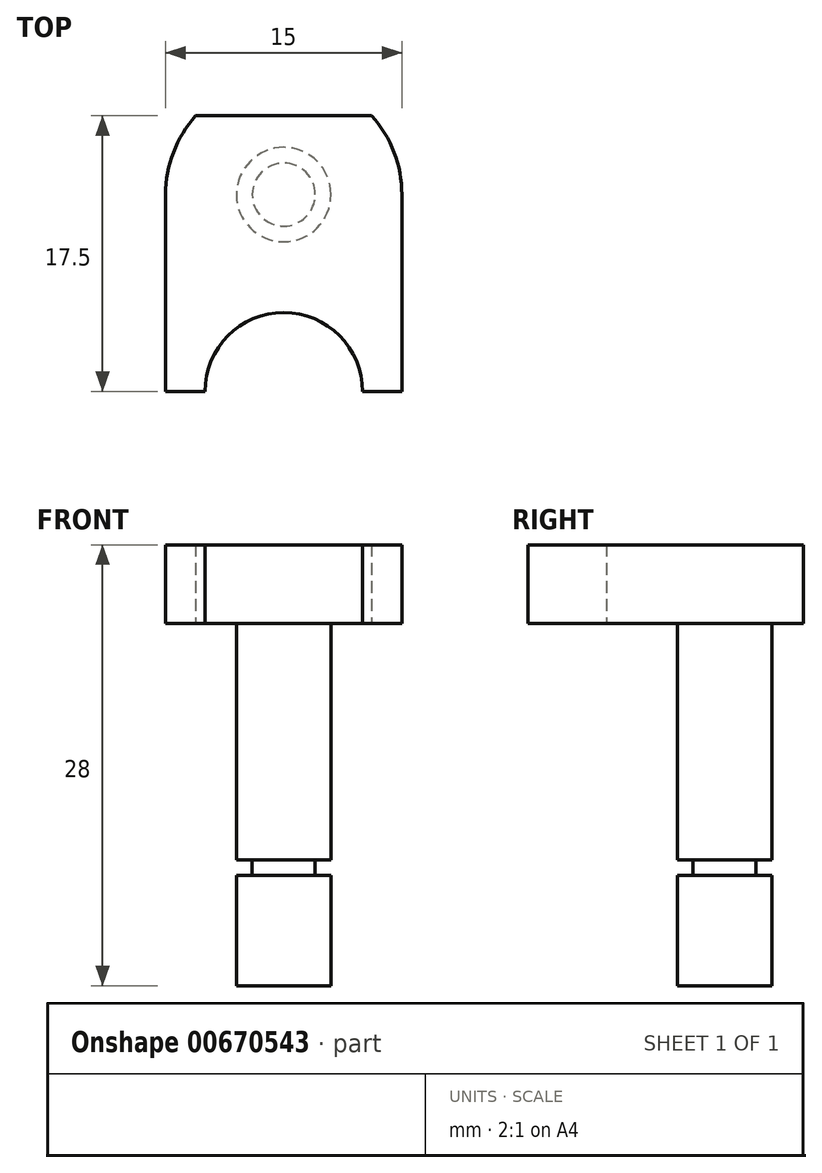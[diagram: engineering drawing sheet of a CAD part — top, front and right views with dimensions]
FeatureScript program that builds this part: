
annotation { "Feature Type Name" : "Feature", "Feature Type Description" : "" }
export const myFeature = defineFeature(function(context is Context, id is Id, definition is map)
    precondition{}
    {
        {
            var Q0;
            Q0=qCreatedBy(makeId("Top.planeOp"),FACE);
            var sketch = newSketch(context, id + "F0", { "sketchPlane" : qUnion([Q0])});
            skCircle(sketch, "E0", {"center": v(0, 0) * mm, "radius": 7.5 * mm});
            skLineSegment(sketch, "E1.bottom", {"start": v(-7.5, 5) * mm, "end": v(7.5, 5) * mm});
            skLineSegment(sketch, "E1.top", {"start": v(-7.5, -7.5) * mm, "end": v(7.5, -7.5) * mm});
            skLineSegment(sketch, "E1.left", {"start": v(-7.5, 5) * mm, "end": v(-7.5, -7.5) * mm});
            skLineSegment(sketch, "E1.right", {"start": v(7.5, 5) * mm, "end": v(7.5, -7.5) * mm});
            skArc(sketch, "E2", {"start": v(5, -12.5) * mm, "mid": v(0, -7.5) * mm, "end": v(-5, -12.5) * mm});
            skLineSegment(sketch, "E3", {"start": v(7.5, -12.5) * mm, "end": v(5, -12.5) * mm});
            skLineSegment(sketch, "E4", {"start": v(7.5, -12.5) * mm, "end": v(7.5, -7.5) * mm});
            skLineSegment(sketch, "E5", {"start": v(-7.5, -7.5) * mm, "end": v(-7.5, -12.5) * mm});
            skLineSegment(sketch, "E6", {"start": v(-7.5, -12.5) * mm, "end": v(-5, -12.5) * mm});
            skSolve(sketch);
        }
        {
            var Q0;
            Q0=makeQuery(id+"F0.imprint","IMPRINT",FACE,{"disambiguationData":[TD([[makeQuery(id+"F0.imprint","IMPRINT",EDGE,{"derivedFrom":sQuery(id+"F0.wireOp",EDGE,"E0")}),1.0]])]});
            var Q1;
            {var subQ0=sQuery(id+"F0.wireOp",EDGE,"E1.right");var subQ1=sQuery(id+"F0.wireOp",EDGE,"E0");var subQ2=makeQuery(id+"F0.imprint","INTERSECT",VERTEX,{"derivedFrom":[subQ1,subQ0]});Q1=makeQuery(id+"F0.imprint","IMPRINT",FACE,{"disambiguationData":[TD([[makeQuery(id+"F0.imprint","IMPRINT",EDGE,{"disambiguationData":[TD([[subQ2,1.0]])],"derivedFrom":subQ1}),-1.0]])]});}
            var Q2;
            {var subQ0=sQuery(id+"F0.wireOp",EDGE,"E1.left");var subQ1=sQuery(id+"F0.wireOp",EDGE,"E0");var subQ2=makeQuery(id+"F0.imprint","INTERSECT",VERTEX,{"derivedFrom":[subQ1,subQ0]});Q2=makeQuery(id+"F0.imprint","IMPRINT",FACE,{"disambiguationData":[TD([[makeQuery(id+"F0.imprint","IMPRINT",EDGE,{"disambiguationData":[TD([[subQ2,-1.0]])],"derivedFrom":subQ1}),-1.0]])]});}
            var Q3;
            {var subQ4=sQuery(id+"F0.wireOp",EDGE,"E3");Q3=makeQuery(id+"F0.imprint","IMPRINT",FACE,{"disambiguationData":[TD([[makeQuery(id+"F0.imprint","IMPRINT",EDGE,{"derivedFrom":subQ4}),-1.0]])]});}
            var Q4;
            {var subQ0=sQuery(id+"F0.wireOp",EDGE,"E5");Q4=makeQuery(id+"F0.imprint","IMPRINT",FACE,{"disambiguationData":[TD([[makeQuery(id+"F0.imprint","IMPRINT",EDGE,{"derivedFrom":subQ0}),1.0]])]});}
            extrude(context, id + "F1", {"entities" : qUnion([Q0, Q1, Q2, Q3, Q4]), "depth" : 5 * mm, "offsetDistance" : 25 * mm});
        }
        {
            var Q0;
            Q0=makeQuery(id+"F1.opExtrude","CAP_FACE",FACE,{"disambiguationData":[OSD([sQuery(id+"F0.wireOp",EDGE,"E0")])],"isStart":true});
            var sketch = newSketch(context, id + "F2", { "sketchPlane" : qUnion([Q0])});
            skCircle(sketch, "E7", {"center": v(0, 0) * mm, "radius": 3 * mm});
            skSolve(sketch);
        }
        {
            var Q0;
            Q0=makeQuery(id+"F2.imprint","IMPRINT",FACE,{"disambiguationData":[TD([[makeQuery(id+"F2.imprint","IMPRINT",EDGE,{"derivedFrom":sQuery(id+"F2.wireOp",EDGE,"E7")}),1.0]])]});
            extrude(context, id + "F3", {"entities" : qUnion([Q0]), "operationType" : NewBodyOperationType.ADD, "depth" : 15 * mm, "offsetDistance" : 25 * mm});
        }
        {
            var Q0;
            Q0=makeQuery(id+"F3.opExtrude","CAP_FACE",FACE,{"disambiguationData":[OSD([sQuery(id+"F2.wireOp",EDGE,"E7")])],"isStart":false});
            var sketch = newSketch(context, id + "F4", { "sketchPlane" : qUnion([Q0])});
            skCircle(sketch, "E8", {"center": v(0, 0) * mm, "radius": 2 * mm});
            skSolve(sketch);
        }
        {
            var Q0;
            Q0=makeQuery(id+"F4.imprint","IMPRINT",FACE,{"disambiguationData":[TD([[makeQuery(id+"F4.imprint","IMPRINT",EDGE,{"derivedFrom":sQuery(id+"F4.wireOp",EDGE,"E8")}),1.0]])]});
            extrude(context, id + "F5", {"entities" : qUnion([Q0]), "operationType" : NewBodyOperationType.ADD, "depth" : 1 * mm, "offsetDistance" : 25 * mm});
        }
        {
            var Q0;
            Q0=makeQuery(id+"F5.opExtrude","CAP_FACE",FACE,{"disambiguationData":[OSD([sQuery(id+"F4.wireOp",EDGE,"E8")])],"isStart":false});
            var sketch = newSketch(context, id + "F6", { "sketchPlane" : qUnion([Q0])});
            skCircle(sketch, "E9", {"center": v(0, 0) * mm, "radius": 3 * mm});
            skSolve(sketch);
        }
        {
            var Q0;
            Q0=makeQuery(id+"F6.imprint","IMPRINT",FACE,{"disambiguationData":[TD([[makeQuery(id+"F6.imprint","IMPRINT",EDGE,{"derivedFrom":sQuery(id+"F6.wireOp",EDGE,"E9")}),1.0]])]});
            var Q1;
            Q1=makeQuery(id+"F6.imprint","IMPRINT",FACE,{"disambiguationData":[TD([[makeQuery(id+"F6.imprint","IMPRINT",EDGE,{"derivedFrom":makeQuery(id+"F5.opExtrude","CAP_EDGE",EDGE,{"disambiguationData":[OSD([sQuery(id+"F4.wireOp",EDGE,"E8")])],"isStart":false})}),1.0]])]});
            extrude(context, id + "F7", {"entities" : qUnion([Q0, Q1]), "operationType" : NewBodyOperationType.ADD, "depth" : 7 * mm, "offsetDistance" : 25 * mm});
        }
    });
